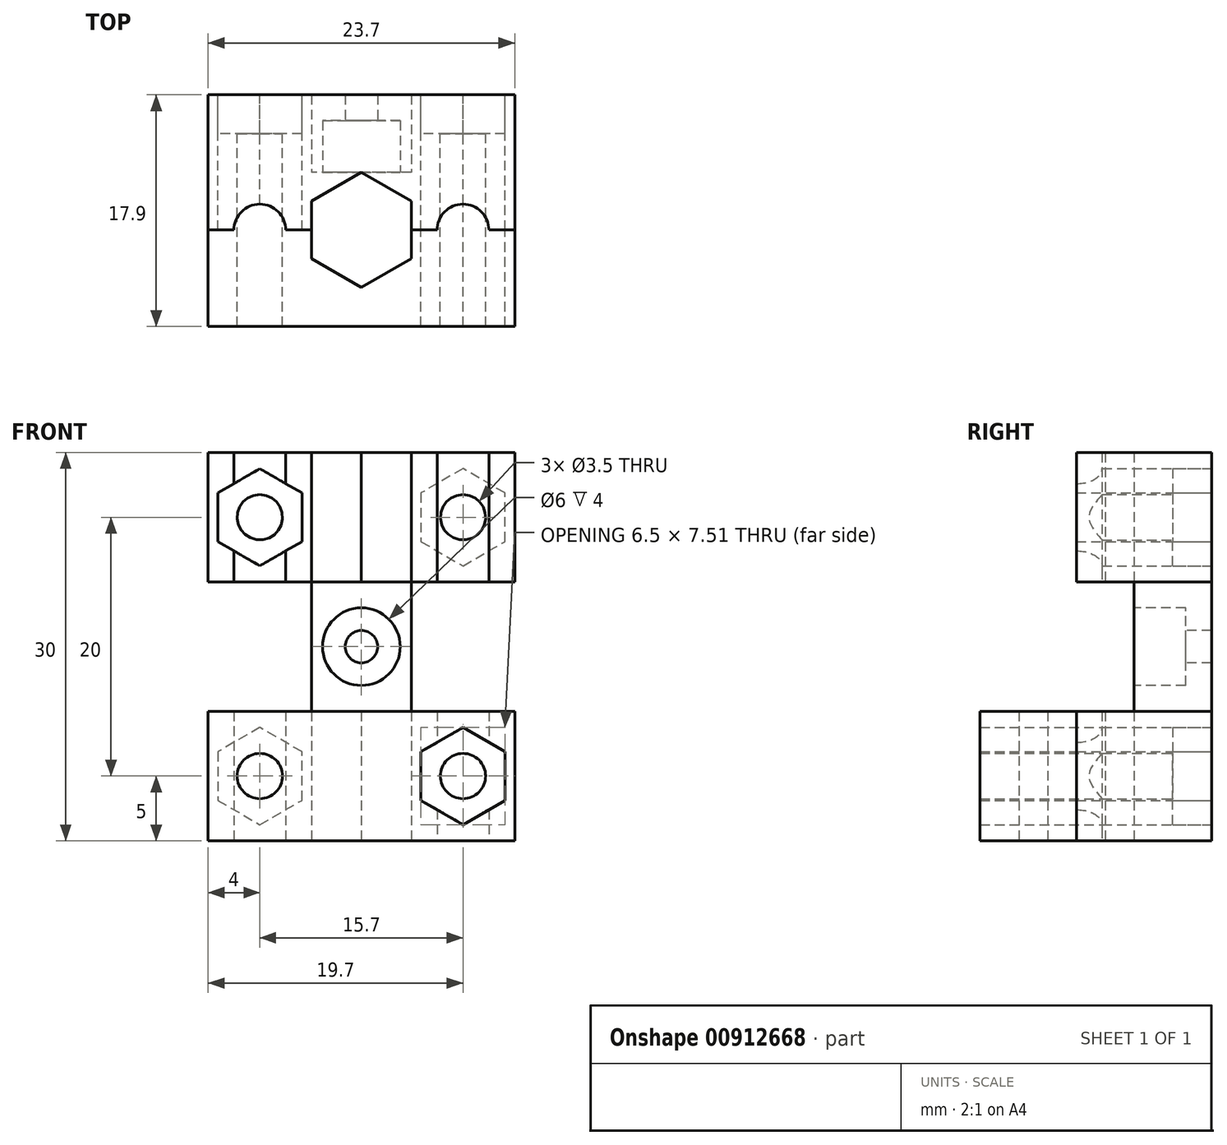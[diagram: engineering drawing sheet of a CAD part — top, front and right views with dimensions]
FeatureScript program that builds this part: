
annotation { "Feature Type Name" : "Feature", "Feature Type Description" : "" }
export const myFeature = defineFeature(function(context is Context, id is Id, definition is map)
    precondition{}
    {
        {
            var Q0;
            Q0=qCreatedBy(makeId("Top.planeOp"),FACE);
            var sketch = newSketch(context, id + "F0", { "sketchPlane" : qUnion([Q0])});
            skCircle(sketch, "E0.cCircle", {"center": v(0, 0) * mm, "radius": 3.85 * mm, "construction": true});
            skLineSegment(sketch, "E0.0", {"start": v(3.85, 2.22) * mm, "end": v(3.85, 0) * mm});
            skLineSegment(sketch, "E0.1", {"start": v(3.85, -2.22) * mm, "end": v(0, -4.45) * mm});
            skLineSegment(sketch, "E0.2", {"start": v(0, -4.45) * mm, "end": v(-3.85, -2.22) * mm});
            skLineSegment(sketch, "E0.3", {"start": v(-3.85, -2.22) * mm, "end": v(-3.85, 0) * mm});
            skLineSegment(sketch, "E0.4", {"start": v(-3.85, 2.22) * mm, "end": v(0, 4.45) * mm});
            skLineSegment(sketch, "E0.5", {"start": v(0, 4.45) * mm, "end": v(3.85, 2.22) * mm});
            skPoint(sketch, "E0.0.midPoint", {"position": v(3.85, 0) * mm});
            skPoint(sketch, "E1", {"position": v(-3.85, 0) * mm});
            skLineSegment(sketch, "E2", {"start": v(-3.85, 0) * mm, "end": v(-3.85, 2.22) * mm});
            skLineSegment(sketch, "E3", {"start": v(3.85, 0) * mm, "end": v(3.85, -2.22) * mm});
            skLineSegment(sketch, "E4", {"start": v(-3.85, 0) * mm, "end": v(-5.85, 0) * mm});
            skLineSegment(sketch, "E5", {"start": v(-11.85, 0) * mm, "end": v(-11.85, 10.45) * mm});
            skLineSegment(sketch, "E6", {"start": v(-11.85, 10.45) * mm, "end": v(0, 10.45) * mm});
            skLineSegment(sketch, "E7", {"start": v(-11.85, 0) * mm, "end": v(-11.85, -7.45) * mm});
            skLineSegment(sketch, "E8", {"start": v(-11.85, -7.45) * mm, "end": v(0, -7.45) * mm});
            skLineSegment(sketch, "E9.MirrorCS", {"start": v(11.85, 10.45) * mm, "end": v(0, 10.45) * mm});
            skLineSegment(sketch, "E10.MirrorCS", {"start": v(11.85, 0) * mm, "end": v(11.85, 10.45) * mm});
            skLineSegment(sketch, "E11.MirrorCS", {"start": v(3.85, 0) * mm, "end": v(5.85, 0) * mm});
            skLineSegment(sketch, "E12.MirrorCS", {"start": v(11.85, -7.45) * mm, "end": v(0, -7.45) * mm});
            skLineSegment(sketch, "E13.MirrorCS", {"start": v(11.85, 0) * mm, "end": v(11.85, -7.45) * mm});
            skLineSegment(sketch, "E14", {"start": v(-9.85, 0) * mm, "end": v(-9.85, 0) * mm});
            skLineSegment(sketch, "E15", {"start": v(-5.85, 0) * mm, "end": v(-5.85, 0) * mm});
            skArc(sketch, "E16", {"start": v(-9.85, 0) * mm, "mid": v(-7.85, 2) * mm, "end": v(-5.85, 0) * mm});
            skLineSegment(sketch, "E17", {"start": v(-9.85, 0) * mm, "end": v(-11.85, 0) * mm});
            skLineSegment(sketch, "E18.MirrorCS", {"start": v(9.85, 0) * mm, "end": v(9.85, 0) * mm});
            skArc(sketch, "E19.MirrorCS", {"start": v(9.85, 0) * mm, "mid": v(7.85, 2) * mm, "end": v(5.85, 0) * mm});
            skLineSegment(sketch, "E20.trimOffspring", {"start": v(9.85, 0) * mm, "end": v(11.85, 0) * mm});
            skSolve(sketch);
        }
        {
            var Q0;
            Q0=makeQuery(id+"F0.imprint","IMPRINT",FACE,{"disambiguationData":[TD([[makeQuery(id+"F0.imprint","IMPRINT",EDGE,{"derivedFrom":sQuery(id+"F0.wireOp",EDGE,"E0.0")}),1.0]])]});
            extrude(context, id + "F1", {"entities" : qUnion([Q0]), "depth" : 30 * mm, "offsetDistance" : 25 * mm});
        }
        {
            var Q0;
            Q0=makeQuery(id+"F1.opExtrude","SWEPT_FACE",FACE,{"disambiguationData":[OSD([sQuery(id+"F0.wireOp",EDGE,"E4")])]});
            var sketch = newSketch(context, id + "F2", { "sketchPlane" : qUnion([Q0])});
            skLineSegment(sketch, "E21.0", {"start": v(-3.85, 30) * mm, "end": v(-3.85, 0) * mm});
            skLineSegment(sketch, "E22.bottom", {"start": v(-11.85, 20) * mm, "end": v(-3.85, 20) * mm});
            skLineSegment(sketch, "E22.top", {"start": v(-11.85, 10) * mm, "end": v(-3.85, 10) * mm});
            skLineSegment(sketch, "E22.left", {"start": v(-11.85, 20) * mm, "end": v(-11.85, 10) * mm});
            skLineSegment(sketch, "E22.right", {"start": v(-3.85, 20) * mm, "end": v(-3.85, 10) * mm});
            skLineSegment(sketch, "E23.MirrorCS", {"start": v(3.85, 20) * mm, "end": v(3.85, 10) * mm});
            skLineSegment(sketch, "E24.MirrorCS", {"start": v(11.85, 20) * mm, "end": v(3.85, 20) * mm});
            skLineSegment(sketch, "E25.MirrorCS", {"start": v(11.85, 20) * mm, "end": v(11.85, 10) * mm});
            skLineSegment(sketch, "E26.MirrorCS", {"start": v(11.85, 10) * mm, "end": v(3.85, 10) * mm});
            skLineSegment(sketch, "E27.0", {"start": v(-11.85, 30) * mm, "end": v(-11.85, 0) * mm});
            skSolve(sketch);
        }
        {
            var Q0;
            Q0 = qSketchRegion(id + "F2", true);
            var Q1;
            Q1=makeQuery(id+"F1.opExtrude","SWEPT_FACE",FACE,{"disambiguationData":[OSD([sQuery(id+"F0.wireOp",EDGE,"E6"),sQuery(id+"F0.wireOp",EDGE,"E9.MirrorCS")])]});
            extrude(context, id + "F3", {"entities" : qUnion([Q0]), "operationType" : NewBodyOperationType.REMOVE, "endBound" : BoundingType.UP_TO_SURFACE, "oppositeDirection" : true, "depth" : 25 * mm, "endBoundEntityFace" : qUnion([Q1]), "offsetDistance" : 25 * mm});
        }
        {
            var Q0;
            {var subQ1=sQuery(id+"F0.wireOp",EDGE,"E4");Q0=makeQuery(id+"F3.boolean.opBoolean","SPLIT",FACE,{"disambiguationData":[TD([makeQuery(id+"F3.opExtrude","SWEPT_FACE",FACE,{"disambiguationData":[OSD([sQuery(id+"F2.wireOp",EDGE,"E22.bottom")])]})])],"derivedFrom":makeQuery(id+"F1.opExtrude","SWEPT_FACE",FACE,{"disambiguationData":[OSD([subQ1])]})});}
            var sketch = newSketch(context, id + "F4", { "sketchPlane" : qUnion([Q0])});
            skLineSegment(sketch, "E28.0", {"start": v(3.85, 20) * mm, "end": v(3.85, 10) * mm});
            skLineSegment(sketch, "E29.0", {"start": v(-3.85, 20) * mm, "end": v(-3.85, 10) * mm});
            skLineSegment(sketch, "E30.bottom", {"start": v(-3.85, 20) * mm, "end": v(3.85, 20) * mm});
            skLineSegment(sketch, "E30.top", {"start": v(-3.85, 10) * mm, "end": v(3.85, 10) * mm});
            skSolve(sketch);
        }
        {
            var Q0;
            Q0 = qSketchRegion(id + "F4", true);
            var Q1;
            Q1=makeQuery(id+"F1.opExtrude","SWEPT_FACE",FACE,{"disambiguationData":[OSD([sQuery(id+"F0.wireOp",EDGE,"E6"),sQuery(id+"F0.wireOp",EDGE,"E9.MirrorCS")])]});
            extrude(context, id + "F5", {"entities" : qUnion([Q0]), "operationType" : NewBodyOperationType.REMOVE, "endBound" : BoundingType.UP_TO_SURFACE, "oppositeDirection" : true, "depth" : 25 * mm, "endBoundEntityFace" : qUnion([Q1]), "hasOffset" : true, "offsetDistance" : 6 * mm});
        }
        {
            var Q0;
            Q0=makeQuery(id+"F5.boolean.opBoolean","COPY",FACE,{"derivedFrom":makeQuery(id+"F5.opExtrude","CAP_FACE",FACE,{"disambiguationData":[OSD([sQuery(id+"F4.wireOp",EDGE,"E30.bottom"),sQuery(id+"F4.wireOp",EDGE,"E30.top"),sQuery(id+"F4.wireOp",EDGE,"E29.0"),sQuery(id+"F4.wireOp",EDGE,"E28.0")])],"isStart":false})});
            var sketch = newSketch(context, id + "F6", { "sketchPlane" : qUnion([Q0])});
            skCircle(sketch, "E31", {"center": v(0, 15) * mm, "radius": 1.25 * mm});
            skPoint(sketch, "E31.centerSnap0", {"position": v(3.85, 15) * mm});
            skSolve(sketch);
        }
        {
            var Q0;
            Q0 = qSketchRegion(id + "F6", true);
            var Q1;
            Q1=makeQuery(id+"F1.opExtrude","SWEPT_FACE",FACE,{"disambiguationData":[OSD([sQuery(id+"F0.wireOp",EDGE,"E6"),sQuery(id+"F0.wireOp",EDGE,"E9.MirrorCS")])]});
            extrude(context, id + "F7", {"entities" : qUnion([Q0]), "operationType" : NewBodyOperationType.REMOVE, "endBound" : BoundingType.UP_TO_SURFACE, "oppositeDirection" : true, "depth" : 25 * mm, "endBoundEntityFace" : qUnion([Q1]), "offsetDistance" : 25 * mm});
        }
        {
            var Q0;
            Q0=makeQuery(id+"F5.boolean.opBoolean","COPY",FACE,{"derivedFrom":makeQuery(id+"F5.opExtrude","CAP_FACE",FACE,{"disambiguationData":[OSD([sQuery(id+"F4.wireOp",EDGE,"E30.bottom"),sQuery(id+"F4.wireOp",EDGE,"E30.top"),sQuery(id+"F4.wireOp",EDGE,"E29.0"),sQuery(id+"F4.wireOp",EDGE,"E28.0")])],"isStart":false})});
            var sketch = newSketch(context, id + "F8", { "sketchPlane" : qUnion([Q0])});
            skCircle(sketch, "E32", {"center": v(0, 15) * mm, "radius": 3 * mm});
            skSolve(sketch);
        }
        {
            var Q0;
            Q0 = qSketchRegion(id + "F8", true);
            extrude(context, id + "F9", {"entities" : qUnion([Q0]), "operationType" : NewBodyOperationType.REMOVE, "oppositeDirection" : true, "depth" : 4 * mm, "offsetDistance" : 25 * mm});
        }
        {
            var Q0;
            Q0=makeQuery(id+"F1.opExtrude","SWEPT_FACE",FACE,{"disambiguationData":[OSD([sQuery(id+"F0.wireOp",EDGE,"E6"),sQuery(id+"F0.wireOp",EDGE,"E9.MirrorCS")])]});
            var sketch = newSketch(context, id + "F10", { "sketchPlane" : qUnion([Q0])});
            skCircle(sketch, "E33.cCircle", {"center": v(-7.85, 25) * mm, "radius": 3.25 * mm, "construction": true});
            skPoint(sketch, "E33.cCircle.centerSnap0", {"position": v(-7.85, 20) * mm});
            skPoint(sketch, "E33.cCircle.centerSnap1", {"position": v(-11.85, 25) * mm});
            skLineSegment(sketch, "E33.0", {"start": v(-4.6, 26.88) * mm, "end": v(-4.6, 23.12) * mm});
            skLineSegment(sketch, "E33.1", {"start": v(-4.6, 23.12) * mm, "end": v(-7.85, 21.25) * mm});
            skLineSegment(sketch, "E33.2", {"start": v(-7.85, 21.25) * mm, "end": v(-11.1, 23.12) * mm});
            skLineSegment(sketch, "E33.3", {"start": v(-11.1, 23.12) * mm, "end": v(-11.1, 26.88) * mm});
            skLineSegment(sketch, "E33.4", {"start": v(-11.1, 26.88) * mm, "end": v(-7.85, 28.75) * mm});
            skLineSegment(sketch, "E33.5", {"start": v(-7.85, 28.75) * mm, "end": v(-4.6, 26.88) * mm});
            skPoint(sketch, "E33.0.midPoint", {"position": v(-4.6, 25) * mm});
            skLineSegment(sketch, "E34", {"start": v(-3.85, 15) * mm, "end": v(3.85, 15) * mm, "construction": true});
            skLineSegment(sketch, "E35.MirrorCS", {"start": v(11.1, 26.88) * mm, "end": v(7.85, 28.75) * mm});
            skLineSegment(sketch, "E36.MirrorCS", {"start": v(4.6, 26.88) * mm, "end": v(4.6, 23.12) * mm});
            skLineSegment(sketch, "E37.MirrorCS", {"start": v(11.1, 23.12) * mm, "end": v(11.1, 26.88) * mm});
            skLineSegment(sketch, "E38.MirrorCS", {"start": v(7.85, 28.75) * mm, "end": v(4.6, 26.88) * mm});
            skLineSegment(sketch, "E39.MirrorCS", {"start": v(4.6, 23.12) * mm, "end": v(7.85, 21.25) * mm});
            skLineSegment(sketch, "E40.MirrorCS", {"start": v(7.85, 21.25) * mm, "end": v(11.1, 23.12) * mm});
            skPoint(sketch, "E41.MirrorP", {"position": v(11.85, 25) * mm});
            skCircle(sketch, "E42.MirrorC", {"center": v(7.85, 25) * mm, "radius": 3.25 * mm, "construction": true});
            skPoint(sketch, "E43.MirrorP", {"position": v(4.6, 25) * mm});
            skLineSegment(sketch, "E44.MirrorCS", {"start": v(11.1, 6.88) * mm, "end": v(11.1, 3.12) * mm});
            skLineSegment(sketch, "E45.MirrorCS", {"start": v(-7.85, 8.75) * mm, "end": v(-11.1, 6.88) * mm});
            skLineSegment(sketch, "E46.MirrorCS", {"start": v(4.6, 3.12) * mm, "end": v(4.6, 6.88) * mm});
            skLineSegment(sketch, "E47.MirrorCS", {"start": v(-4.6, 6.88) * mm, "end": v(-7.85, 8.75) * mm});
            skLineSegment(sketch, "E48.MirrorCS", {"start": v(11.1, 3.12) * mm, "end": v(7.85, 1.25) * mm});
            skLineSegment(sketch, "E49.MirrorCS", {"start": v(-4.6, 3.12) * mm, "end": v(-4.6, 6.88) * mm});
            skLineSegment(sketch, "E50.MirrorCS", {"start": v(-11.1, 3.12) * mm, "end": v(-7.85, 1.25) * mm});
            skLineSegment(sketch, "E51.MirrorCS", {"start": v(7.85, 8.75) * mm, "end": v(11.1, 6.88) * mm});
            skLineSegment(sketch, "E52.MirrorCS", {"start": v(4.6, 6.88) * mm, "end": v(7.85, 8.75) * mm});
            skLineSegment(sketch, "E53.MirrorCS", {"start": v(-7.85, 1.25) * mm, "end": v(-4.6, 3.12) * mm});
            skLineSegment(sketch, "E54.MirrorCS", {"start": v(-11.1, 6.88) * mm, "end": v(-11.1, 3.12) * mm});
            skPoint(sketch, "E55.MirrorP", {"position": v(4.6, 5) * mm});
            skPoint(sketch, "E56.MirrorP", {"position": v(11.85, 5) * mm});
            skLineSegment(sketch, "E57.MirrorCS", {"start": v(7.85, 1.25) * mm, "end": v(4.6, 3.12) * mm});
            skPoint(sketch, "E58.MirrorP", {"position": v(-7.85, 10) * mm});
            skCircle(sketch, "E59.MirrorC", {"center": v(7.85, 5) * mm, "radius": 3.25 * mm, "construction": true});
            skCircle(sketch, "E60.MirrorC", {"center": v(-7.85, 5) * mm, "radius": 3.25 * mm, "construction": true});
            skPoint(sketch, "E61.MirrorP", {"position": v(-4.6, 5) * mm});
            skPoint(sketch, "E62.MirrorP", {"position": v(-11.85, 5) * mm});
            skSolve(sketch);
        }
        {
            var Q0;
            Q0 = qSketchRegion(id + "F10", true);
            extrude(context, id + "F11", {"entities" : qUnion([Q0]), "operationType" : NewBodyOperationType.REMOVE, "oppositeDirection" : true, "depth" : 3 * mm, "offsetDistance" : 25 * mm});
        }
        {
            var Q0;
            Q0=makeQuery(id+"F1.opExtrude","SWEPT_FACE",FACE,{"disambiguationData":[OSD([sQuery(id+"F0.wireOp",EDGE,"E6"),sQuery(id+"F0.wireOp",EDGE,"E9.MirrorCS")])]});
            var sketch = newSketch(context, id + "F12", { "sketchPlane" : qUnion([Q0])});
            skCircle(sketch, "E63", {"center": v(-7.85, 25) * mm, "radius": 1.75 * mm});
            skPoint(sketch, "E63.centerSnap0", {"position": v(-11.85, 25) * mm});
            skCircle(sketch, "E64.MirrorC", {"center": v(7.85, 25) * mm, "radius": 1.75 * mm});
            skCircle(sketch, "E65.MirrorC", {"center": v(7.85, 5) * mm, "radius": 1.75 * mm});
            skCircle(sketch, "E66.MirrorC", {"center": v(-7.85, 5) * mm, "radius": 1.75 * mm});
            skSolve(sketch);
        }
        {
            var Q0;
            Q0=makeQuery(id+"F0.imprint","IMPRINT",FACE,{"disambiguationData":[TD([[makeQuery(id+"F0.imprint","IMPRINT",EDGE,{"derivedFrom":sQuery(id+"F0.wireOp",EDGE,"E0.1")}),1.0]])]});
            var Q1;
            Q1=makeQuery(id+"F5.boolean.opBoolean","MERGE",FACE,{"derivedFrom":[makeQuery(id+"F3.boolean.opBoolean","COPY",FACE,{"derivedFrom":makeQuery(id+"F3.opExtrude","SWEPT_FACE",FACE,{"disambiguationData":[OSD([sQuery(id+"F2.wireOp",EDGE,"E26.MirrorCS")])]})})],"fromTools":[makeQuery(id+"F5.opExtrude","SWEPT_FACE",FACE,{"disambiguationData":[OSD([sQuery(id+"F4.wireOp",EDGE,"E30.top")])]})]});
            extrude(context, id + "F13", {"entities" : qUnion([Q0]), "endBound" : BoundingType.UP_TO_SURFACE, "depth" : 25 * mm, "endBoundEntityFace" : qUnion([Q1]), "offsetDistance" : 25 * mm});
        }
        {
            var Q0;
            Q0=makeQuery(id+"F12.imprint","IMPRINT",FACE,{"disambiguationData":[TD([[makeQuery(id+"F12.imprint","IMPRINT",EDGE,{"derivedFrom":sQuery(id+"F12.wireOp",EDGE,"E63")}),1.0]])]});
            var Q1;
            Q1=makeQuery(id+"F12.imprint","IMPRINT",FACE,{"disambiguationData":[TD([[makeQuery(id+"F12.imprint","IMPRINT",EDGE,{"derivedFrom":sQuery(id+"F12.wireOp",EDGE,"E64.MirrorC")}),-1.0]])]});
            var Q2;
            Q2=makeQuery(id+"F12.imprint","IMPRINT",FACE,{"disambiguationData":[TD([[makeQuery(id+"F12.imprint","IMPRINT",EDGE,{"derivedFrom":sQuery(id+"F12.wireOp",EDGE,"E65.MirrorC")}),1.0]])]});
            var Q3;
            Q3=makeQuery(id+"F12.imprint","IMPRINT",FACE,{"disambiguationData":[TD([[makeQuery(id+"F12.imprint","IMPRINT",EDGE,{"derivedFrom":sQuery(id+"F12.wireOp",EDGE,"E66.MirrorC")}),-1.0]])]});
            var Q4;
            Q4=makeQuery(id+"F13.opExtrude","SWEPT_FACE",FACE,{"disambiguationData":[OSD([sQuery(id+"F0.wireOp",EDGE,"E8"),sQuery(id+"F0.wireOp",EDGE,"E12.MirrorCS")])]});
            extrude(context, id + "F14", {"entities" : qUnion([Q0, Q1, Q2, Q3]), "operationType" : NewBodyOperationType.REMOVE, "endBound" : BoundingType.UP_TO_SURFACE, "oppositeDirection" : true, "depth" : 25 * mm, "endBoundEntityFace" : qUnion([Q4]), "offsetDistance" : 25 * mm});
        }
    });
